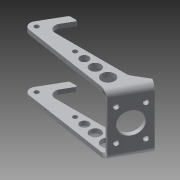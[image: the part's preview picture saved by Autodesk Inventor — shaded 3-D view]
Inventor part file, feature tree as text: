
AUTODESK INVENTOR PART (.ipt)
format: ipt  version: 2013 (Build 170138000, 138)  size: 1,920,512 bytes
history: native  units: in
note: dims shown in document units (in); Inventor stores cm internally (conversion verified against a paired STEP export)
features: sheet_metal_op x4, other x4, sketch x3, mirror x1, chamfer x1
ambient origin geometry x8: Origin, YZ Plane, XZ Plane, XY Plane, X Axis, Y Axis, Z Axis, Center Point
bodies: Solid1 (feature_tree)
feature tree (13):
  sheet_metal_op  "Face1"
  sheet_metal_op  "Flange1"
  mirror  "Mirror1"
  chamfer  "Corner Round1"
  sketch  "Sketch1"  dims[d7=0.375in]
  other  "Plate1"
  sketch  "Sketch2"  dims[d8=0.375in]
  other  "Plate2"
  sheet_metal_op  "Bend1"
  sheet_metal_op  "Corner1"
  sketch  "Sketch3"  dims[d10=0.4278in d11=0.125in d12=0.4722in d13=60.0deg d14=0.7647in d19=1.6084in d20=0.5in d21=0.25in d22=0.25in d23=0.125in d24=0.5in d25=0.25in d26=1.75in d27=90.0deg d28=0.1in d29=1.0in d30=0.25in d31=0.25in d32=2.8in d33=0.266in d34=1.8in d35=2.1084in d36=0.3667in d37=0.7874in d39=1.8in d40=0.7874in d42=1.25in d45=0.25in d46=0.0in d64=1.0in d66=0.5in d67=0.375in d68=0.375in d69=1.9834in d71=4.0549in d72=0.5774in d73=0.6in d74=0.75in d75=0.625in d76=0.5in d77=1.0in d78=1.875in d79=2.625in d80=0.0625in d81=120.0deg d82=1.25in d83=0.266in d84=0.266in d85=3.25in d86=1.25in]
  other  "Cut1"
  other  "Definition1"
